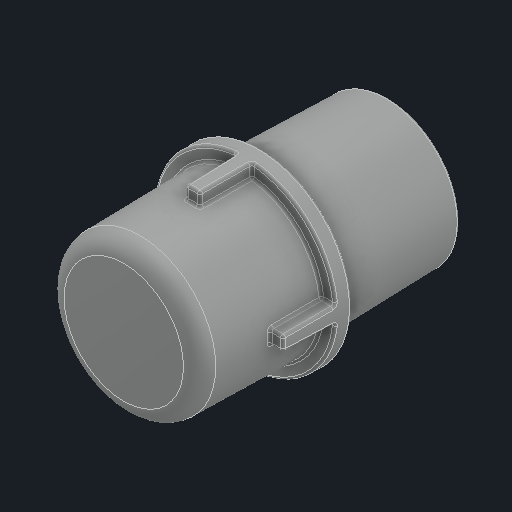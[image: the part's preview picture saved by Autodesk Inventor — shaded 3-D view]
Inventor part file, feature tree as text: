
AUTODESK INVENTOR PART (.ipt)
format: ipt  version: 2024.2 (Build 282272000, 272)  size: 359,424 bytes
history: native  units: in
note: dims shown in document units (in); Inventor stores cm internally (conversion verified against a paired STEP export)
features: fillet x1
ambient origin geometry x8: Origin, YZ Plane, XZ Plane, XY Plane, X Axis, Y Axis, Z Axis, Center Point
bodies: Solid1 (feature_tree)
feature tree (1):
  fillet  "Fillet3"  [1 undecoded]
note: 1 required parameter value undecoded (feature->parameter linkage not recoverable at this tier; creation-order binding heuristic only, values carry confidence <= 0.55)
